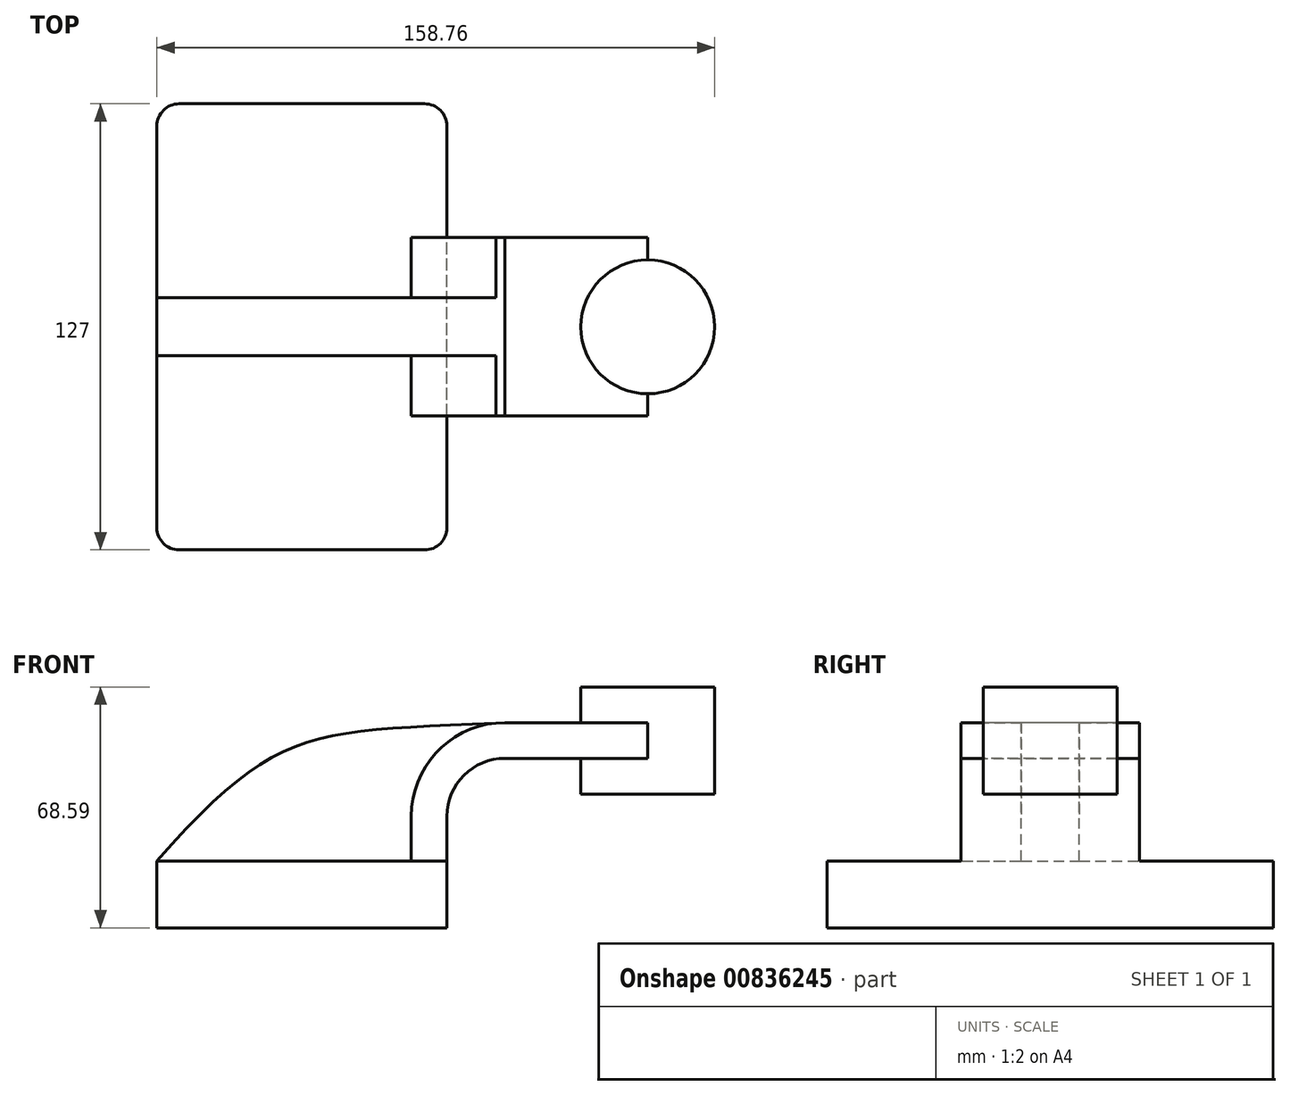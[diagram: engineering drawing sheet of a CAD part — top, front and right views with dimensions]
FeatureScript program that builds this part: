
annotation { "Feature Type Name" : "Feature", "Feature Type Description" : "" }
export const myFeature = defineFeature(function(context is Context, id is Id, definition is map)
    precondition{}
    {
        {
            var Q0;
            Q0=qCreatedBy(makeId("Front.planeOp"),FACE);
            var sketch = newSketch(context, id + "F0", { "sketchPlane" : qUnion([Q0])});
            skLineSegment(sketch, "E0.bottom", {"start": v(41.28, -9.52) * mm, "end": v(-41.27, -9.53) * mm});
            skLineSegment(sketch, "E0.top", {"start": v(41.27, 9.53) * mm, "end": v(-41.27, 9.53) * mm});
            skLineSegment(sketch, "E0.left", {"start": v(41.28, -9.52) * mm, "end": v(41.27, 9.53) * mm});
            skLineSegment(sketch, "E0.right", {"start": v(-41.27, -9.53) * mm, "end": v(-41.27, 9.53) * mm});
            skPoint(sketch, "E0.middle", {"position": v(0, 0) * mm});
            skLineSegment(sketch, "E1.bottom", {"start": v(117.48, 28.58) * mm, "end": v(79.38, 28.58) * mm});
            skLineSegment(sketch, "E1.top", {"start": v(117.48, 59.06) * mm, "end": v(79.38, 59.06) * mm});
            skLineSegment(sketch, "E1.left", {"start": v(117.48, 28.58) * mm, "end": v(117.48, 59.06) * mm});
            skLineSegment(sketch, "E1.right", {"start": v(79.38, 28.58) * mm, "end": v(79.38, 59.06) * mm});
            skPoint(sketch, "E1.middle", {"position": v(98.43, 43.82) * mm});
            skPoint(sketch, "E2.endSnap0", {"position": v(0, 9.53) * mm});
            skLineSegment(sketch, "E3", {"start": v(41.27, 9.53) * mm, "end": v(41.27, 22.23) * mm});
            skArc(sketch, "E4", {"start": v(41.27, 22.23) * mm, "mid": v(46.11, 33.9) * mm, "end": v(57.78, 38.74) * mm});
            skLineSegment(sketch, "E5", {"start": v(57.78, 38.74) * mm, "end": v(98.43, 38.74) * mm});
            skLineSegment(sketch, "E6.0", {"start": v(57.78, 48.9) * mm, "end": v(98.43, 48.9) * mm});
            skArc(sketch, "E6.1", {"start": v(31.11, 22.23) * mm, "mid": v(38.93, 41.08) * mm, "end": v(57.78, 48.9) * mm});
            skLineSegment(sketch, "E6.2", {"start": v(31.11, 9.53) * mm, "end": v(31.11, 22.23) * mm});
            skLineSegment(sketch, "E7", {"start": v(98.43, 28.58) * mm, "end": v(98.43, 59.06) * mm});
            skFitSpline(sketch, "E8", {"points": [v(-41.27, 9.52) * mm, v(57.78, 48.9) * mm], "startDerivative": vector(104.17, 117.22) * mm, "endDerivative": vector(167.98, 8.1) * mm});
            skSolve(sketch);
        }
        {
            var Q0;
            Q0=makeQuery(id+"F0.imprint","IMPRINT",FACE,{"disambiguationData":[TD([[makeQuery(id+"F0.imprint","IMPRINT",EDGE,{"derivedFrom":sQuery(id+"F0.wireOp",EDGE,"E0.bottom")}),-1.0]])]});
            extrude(context, id + "F1", {"entities" : qUnion([Q0]), "endBound" : BoundingType.SYMMETRIC, "depth" : 127 * mm, "offsetDistance" : 25.4 * mm});
        }
        {
            var Q0;
            {var subQ1=sQuery(id+"F0.wireOp",EDGE,"E3");Q0=makeQuery(id+"F0.imprint","IMPRINT",FACE,{"disambiguationData":[TD([[makeQuery(id+"F0.imprint","IMPRINT",EDGE,{"derivedFrom":subQ1}),1.0]])]});}
            var Q1;
            {var subQ0=sQuery(id+"F0.wireOp",EDGE,"E5");var subQ1=sQuery(id+"F0.wireOp",EDGE,"E1.right");var subQ2=makeQuery(id+"F0.imprint","INTERSECT",VERTEX,{"derivedFrom":[subQ1,subQ0]});Q1=makeQuery(id+"F0.imprint","IMPRINT",FACE,{"disambiguationData":[TD([[makeQuery(id+"F0.imprint","IMPRINT",EDGE,{"disambiguationData":[TD([[subQ2,-1.0]])],"derivedFrom":subQ1}),-1.0]])]});}
            extrude(context, id + "F2", {"entities" : qUnion([Q0, Q1]), "operationType" : NewBodyOperationType.ADD, "endBound" : BoundingType.SYMMETRIC, "depth" : 50.8 * mm, "offsetDistance" : 25.4 * mm});
        }
        {
            var Q0;
            {var subQ3=sQuery(id+"F0.wireOp",EDGE,"E6.2");Q0=makeQuery(id+"F0.imprint","IMPRINT",FACE,{"disambiguationData":[TD([[makeQuery(id+"F0.imprint","IMPRINT",EDGE,{"derivedFrom":subQ3}),1.0]])]});}
            extrude(context, id + "F3", {"entities" : qUnion([Q0]), "operationType" : NewBodyOperationType.ADD, "endBound" : BoundingType.SYMMETRIC, "depth" : 16.5 * mm, "offsetDistance" : 25.4 * mm});
        }
        {
            var Q0;
            {var subQ0=sQuery(id+"F0.wireOp",EDGE,"E1.left");Q0=makeQuery(id+"F0.imprint","IMPRINT",FACE,{"disambiguationData":[TD([[makeQuery(id+"F0.imprint","IMPRINT",EDGE,{"derivedFrom":subQ0}),1.0]])]});}
            var Q1;
            Q1=sQuery(id+"F0.wireOp",EDGE,"E7");
            revolve(context, id + "F4", {"operationType" : NewBodyOperationType.ADD, "surfaceOperationType" : NewSurfaceOperationType.NEW, "entities" : qUnion([Q0]), "axis" : qUnion([Q1]), "revolveType" : RevolveType.FULL});
        }
        {
            var Q0;
            Q0=makeQuery(id+"F1.opExtrude","CAP_EDGE",EDGE,{"disambiguationData":[OSD([sQuery(id+"F0.wireOp",EDGE,"E0.right")])],"isStart":false});
            var Q1;
            Q1=makeQuery(id+"F1.opExtrude","CAP_EDGE",EDGE,{"disambiguationData":[OSD([sQuery(id+"F0.wireOp",EDGE,"E0.left")])],"isStart":false});
            var Q2;
            Q2=makeQuery(id+"F1.opExtrude","CAP_EDGE",EDGE,{"disambiguationData":[OSD([sQuery(id+"F0.wireOp",EDGE,"E0.left")])],"isStart":true});
            var Q3;
            Q3=makeQuery(id+"F1.opExtrude","CAP_EDGE",EDGE,{"disambiguationData":[OSD([sQuery(id+"F0.wireOp",EDGE,"E0.right")])],"isStart":true});
            fillet(context, id + "F5", {"entities" : qUnion([Q0, Q1, Q2, Q3]), "radius" : 6.35 * mm, "tangentPropagation" : true, "allowEdgeOverflow" : false});
        }
    });
